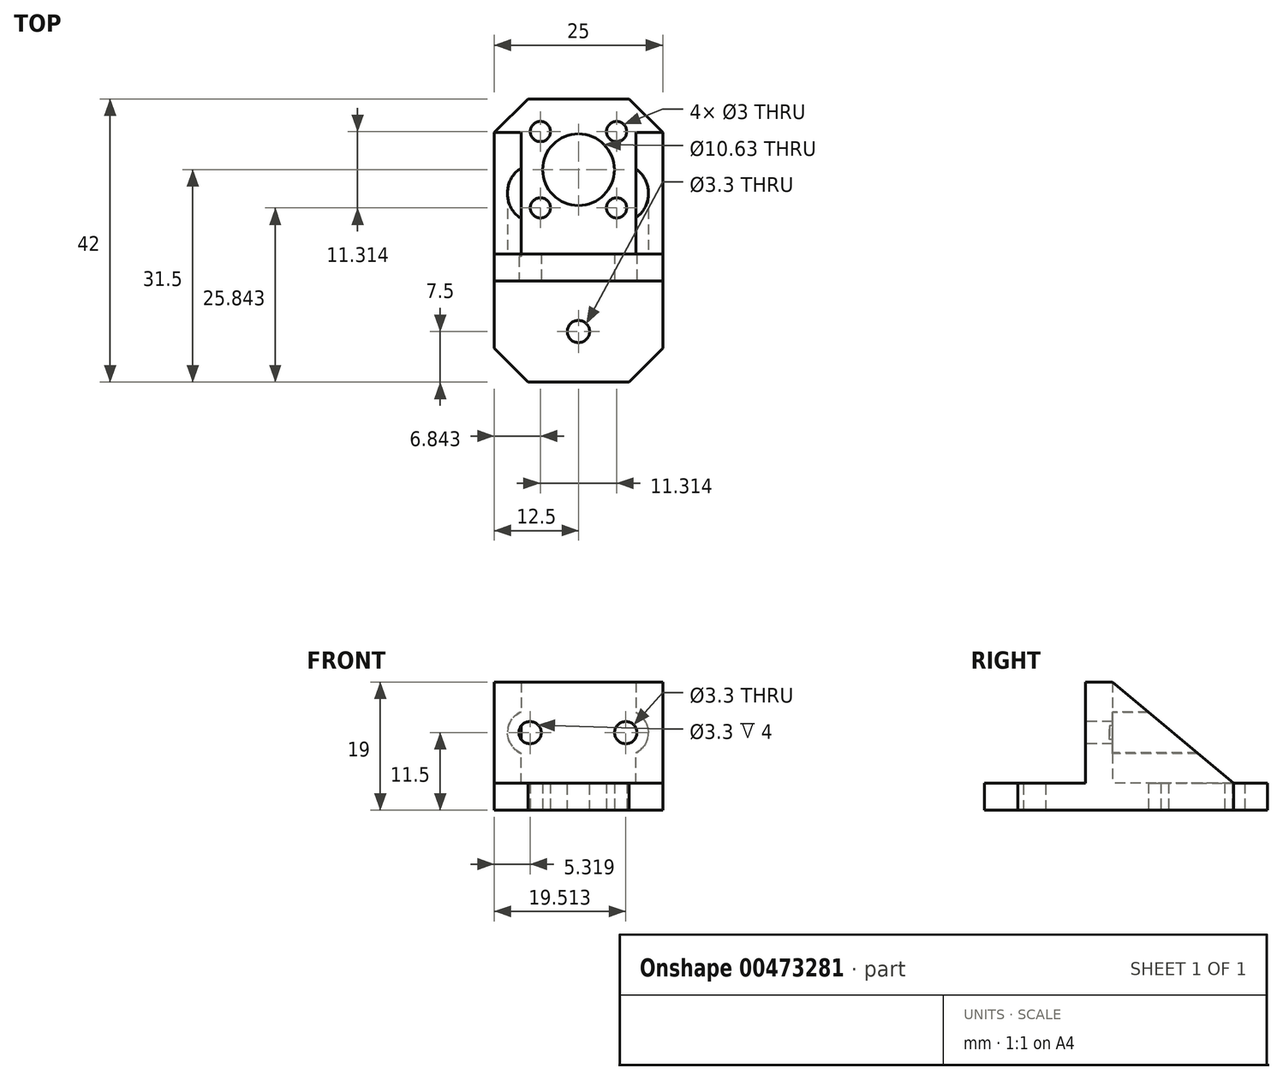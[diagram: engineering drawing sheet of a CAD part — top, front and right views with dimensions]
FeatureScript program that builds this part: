
annotation { "Feature Type Name" : "Feature", "Feature Type Description" : "" }
export const myFeature = defineFeature(function(context is Context, id is Id, definition is map)
    precondition{}
    {
        {
            var Q0;
            Q0=qCreatedBy(makeId("Top.planeOp"),FACE);
            var sketch = newSketch(context, id + "F0", { "sketchPlane" : qUnion([Q0])});
            skCircle(sketch, "E0.0", {"center": v(-5.66, 5.66) * mm, "radius": 1.5 * mm});
            skCircle(sketch, "E1.0", {"center": v(5.66, 5.66) * mm, "radius": 1.5 * mm});
            skCircle(sketch, "E2.0", {"center": v(0, 0) * mm, "radius": 5.32 * mm});
            skCircle(sketch, "E3.0", {"center": v(-5.66, -5.66) * mm, "radius": 1.5 * mm});
            skCircle(sketch, "E4.0", {"center": v(5.66, -5.66) * mm, "radius": 1.5 * mm});
            skLineSegment(sketch, "E5.MirrorCS", {"start": v(12.5, 10.5) * mm, "end": v(12.5, -10.5) * mm});
            skLineSegment(sketch, "E6.MirrorCS", {"start": v(10.5, -12.5) * mm, "end": v(-10.5, -12.5) * mm});
            skLineSegment(sketch, "E7.MirrorCS", {"start": v(-12.5, 10.5) * mm, "end": v(-12.5, -10.5) * mm});
            skPoint(sketch, "E8.visualSharp", {"position": v(-12.5, 12.5) * mm});
            skPoint(sketch, "E9.visualSharp", {"position": v(12.5, 12.5) * mm});
            skPoint(sketch, "E10.visualSharp", {"position": v(12.5, -12.5) * mm});
            skArc(sketch, "E10.filletArc", {"start": v(10.5, -12.5) * mm, "mid": v(11.91, -11.91) * mm, "end": v(12.5, -10.5) * mm});
            skPoint(sketch, "E11.visualSharp", {"position": v(-12.5, -12.5) * mm});
            skArc(sketch, "E11.filletArc", {"start": v(-12.5, -10.5) * mm, "mid": v(-11.91, -11.91) * mm, "end": v(-10.5, -12.5) * mm});
            skLineSegment(sketch, "E12.0", {"start": v(10.5, -16.5) * mm, "end": v(-10.5, -16.5) * mm});
            skLineSegment(sketch, "E13", {"start": v(-12.5, -10.5) * mm, "end": v(-12.5, -16.5) * mm});
            skLineSegment(sketch, "E14", {"start": v(-12.5, -16.5) * mm, "end": v(-10.5, -16.5) * mm});
            skLineSegment(sketch, "E15", {"start": v(10.5, -16.5) * mm, "end": v(12.5, -16.5) * mm});
            skLineSegment(sketch, "E16", {"start": v(12.5, -16.5) * mm, "end": v(12.5, -10.5) * mm});
            skLineSegment(sketch, "E17.bottom", {"start": v(-12.5, 10.5) * mm, "end": v(12.5, 10.5) * mm});
            skLineSegment(sketch, "E17.left", {"start": v(-12.5, 10.5) * mm, "end": v(-12.5, 10.5) * mm});
            skLineSegment(sketch, "E17.right", {"start": v(12.5, 10.5) * mm, "end": v(12.5, 10.5) * mm});
            skSolve(sketch);
        }
        {
            var Q0;
            Q0 = qSketchRegion(id + "F0", true);
            extrude(context, id + "F1", {"entities" : qUnion([Q0]), "depth" : 4 * mm, "offsetDistance" : 25 * mm});
        }
        {
            var Q0;
            Q0=makeQuery(id+"F1.opExtrude","SWEPT_EDGE",EDGE,{"disambiguationData":[OSD([sQuery(id+"F0.wireOp",EDGE,"E5.MirrorCS"),sQuery(id+"F0.wireOp",EDGE,"E17.bottom")])]});
            var Q1;
            Q1=makeQuery(id+"F1.opExtrude","SWEPT_EDGE",EDGE,{"disambiguationData":[OSD([sQuery(id+"F0.wireOp",EDGE,"E7.MirrorCS"),sQuery(id+"F0.wireOp",EDGE,"E17.bottom")])]});
            chamfer(context, id + "F2", {"entities" : qUnion([Q0, Q1]), "width" : 5 * mm, "tangentPropagation" : true});
        }
        {
            var Q0;
            Q0=makeQuery(id+"F1.opExtrude","CAP_FACE",FACE,{"disambiguationData":[OSD([sQuery(id+"F0.wireOp",EDGE,"E0.0"),sQuery(id+"F0.wireOp",EDGE,"E1.0"),sQuery(id+"F0.wireOp",EDGE,"E2.0"),sQuery(id+"F0.wireOp",EDGE,"E3.0"),sQuery(id+"F0.wireOp",EDGE,"E4.0"),sQuery(id+"F0.wireOp",EDGE,"E5.MirrorCS"),sQuery(id+"F0.wireOp",EDGE,"E7.MirrorCS"),sQuery(id+"F0.wireOp",EDGE,"E12.0"),sQuery(id+"F0.wireOp",EDGE,"E13"),sQuery(id+"F0.wireOp",EDGE,"E14"),sQuery(id+"F0.wireOp",EDGE,"E15"),sQuery(id+"F0.wireOp",EDGE,"E16"),sQuery(id+"F0.wireOp",EDGE,"E17.bottom")])],"isStart":false});
            var sketch = newSketch(context, id + "F3", { "sketchPlane" : qUnion([Q0])});
            skLineSegment(sketch, "E18.bottom", {"start": v(-12.5, -16.5) * mm, "end": v(12.5, -16.5) * mm});
            skLineSegment(sketch, "E18.top", {"start": v(-12.5, -12.5) * mm, "end": v(12.5, -12.5) * mm});
            skLineSegment(sketch, "E18.left", {"start": v(-12.5, -16.5) * mm, "end": v(-12.5, -12.5) * mm});
            skLineSegment(sketch, "E18.right", {"start": v(12.5, -16.5) * mm, "end": v(12.5, -12.5) * mm});
            skSolve(sketch);
        }
        {
            var Q0;
            Q0 = qSketchRegion(id + "F3", true);
            extrude(context, id + "F4", {"entities" : qUnion([Q0]), "operationType" : NewBodyOperationType.ADD, "depth" : 15 * mm, "offsetDistance" : 25 * mm});
        }
        {
            var Q0;
            Q0=makeQuery(id+"F1.opExtrude","CAP_FACE",FACE,{"disambiguationData":[OSD([sQuery(id+"F0.wireOp",EDGE,"E0.0"),sQuery(id+"F0.wireOp",EDGE,"E1.0"),sQuery(id+"F0.wireOp",EDGE,"E2.0"),sQuery(id+"F0.wireOp",EDGE,"E3.0"),sQuery(id+"F0.wireOp",EDGE,"E4.0"),sQuery(id+"F0.wireOp",EDGE,"E5.MirrorCS"),sQuery(id+"F0.wireOp",EDGE,"E7.MirrorCS"),sQuery(id+"F0.wireOp",EDGE,"E12.0"),sQuery(id+"F0.wireOp",EDGE,"E13"),sQuery(id+"F0.wireOp",EDGE,"E14"),sQuery(id+"F0.wireOp",EDGE,"E15"),sQuery(id+"F0.wireOp",EDGE,"E16"),sQuery(id+"F0.wireOp",EDGE,"E17.bottom")])],"isStart":true});
            var sketch = newSketch(context, id + "F5", { "sketchPlane" : qUnion([Q0])});
            skLineSegment(sketch, "E19.bottom", {"start": v(-12.5, 16.5) * mm, "end": v(12.5, 16.5) * mm});
            skLineSegment(sketch, "E19.top", {"start": v(-12.5, 31.5) * mm, "end": v(12.5, 31.5) * mm});
            skLineSegment(sketch, "E19.left", {"start": v(-12.5, 16.5) * mm, "end": v(-12.5, 31.5) * mm});
            skLineSegment(sketch, "E19.right", {"start": v(12.5, 16.5) * mm, "end": v(12.5, 31.5) * mm});
            skSolve(sketch);
        }
        {
            var Q0;
            Q0 = qSketchRegion(id + "F5", true);
            extrude(context, id + "F6", {"entities" : qUnion([Q0]), "operationType" : NewBodyOperationType.ADD, "oppositeDirection" : true, "depth" : 4 * mm, "offsetDistance" : 25 * mm});
        }
        {
            var Q0;
            Q0=makeQuery(id+"F4.boolean.opBoolean","MERGE",FACE,{"derivedFrom":[makeQuery(id+"F1.opExtrude","SWEPT_FACE",FACE,{"disambiguationData":[OSD([sQuery(id+"F0.wireOp",EDGE,"E12.0"),sQuery(id+"F0.wireOp",EDGE,"E14"),sQuery(id+"F0.wireOp",EDGE,"E15")])]}),makeQuery(id+"F4.opExtrude","SWEPT_FACE",FACE,{"disambiguationData":[OSD([sQuery(id+"F3.wireOp",EDGE,"E18.bottom")])]})]});
            var sketch = newSketch(context, id + "F7", { "sketchPlane" : qUnion([Q0])});
            skCircle(sketch, "E20", {"center": v(-7.18, 11.5) * mm, "radius": 1.65 * mm});
            skPoint(sketch, "E20.centerSnap0", {"position": v(-12.5, 11.5) * mm});
            skCircle(sketch, "E21", {"center": v(7.01, 11.5) * mm, "radius": 1.65 * mm});
            skSolve(sketch);
        }
        {
            var Q0;
            Q0 = qSketchRegion(id + "F7", true);
            extrude(context, id + "F8", {"entities" : qUnion([Q0]), "operationType" : NewBodyOperationType.REMOVE, "oppositeDirection" : true, "depth" : 25 * mm, "offsetDistance" : 25 * mm});
        }
        {
            var Q0;
            Q0=makeQuery(id+"F6.opExtrude","CAP_FACE",FACE,{"disambiguationData":[OSD([sQuery(id+"F5.wireOp",EDGE,"E19.bottom"),sQuery(id+"F5.wireOp",EDGE,"E19.top"),sQuery(id+"F5.wireOp",EDGE,"E19.left"),sQuery(id+"F5.wireOp",EDGE,"E19.right")])],"isStart":false});
            var sketch = newSketch(context, id + "F9", { "sketchPlane" : qUnion([Q0])});
            skCircle(sketch, "E22", {"center": v(0, -24) * mm, "radius": 1.65 * mm});
            skPoint(sketch, "E22.centerSnap0", {"position": v(0, -31.5) * mm});
            skPoint(sketch, "E22.centerSnap1", {"position": v(-12.5, -24) * mm});
            skSolve(sketch);
        }
        {
            var Q0;
            Q0 = qSketchRegion(id + "F9", true);
            extrude(context, id + "F10", {"entities" : qUnion([Q0]), "operationType" : NewBodyOperationType.REMOVE, "oppositeDirection" : true, "depth" : 25 * mm, "offsetDistance" : 25 * mm});
        }
        {
            var Q0;
            Q0=makeQuery(id+"F1.opExtrude","CAP_FACE",FACE,{"disambiguationData":[OSD([sQuery(id+"F0.wireOp",EDGE,"E0.0"),sQuery(id+"F0.wireOp",EDGE,"E1.0"),sQuery(id+"F0.wireOp",EDGE,"E2.0"),sQuery(id+"F0.wireOp",EDGE,"E3.0"),sQuery(id+"F0.wireOp",EDGE,"E4.0"),sQuery(id+"F0.wireOp",EDGE,"E5.MirrorCS"),sQuery(id+"F0.wireOp",EDGE,"E7.MirrorCS"),sQuery(id+"F0.wireOp",EDGE,"E12.0"),sQuery(id+"F0.wireOp",EDGE,"E13"),sQuery(id+"F0.wireOp",EDGE,"E14"),sQuery(id+"F0.wireOp",EDGE,"E15"),sQuery(id+"F0.wireOp",EDGE,"E16"),sQuery(id+"F0.wireOp",EDGE,"E17.bottom")])],"isStart":false});
            var sketch = newSketch(context, id + "F11", { "sketchPlane" : qUnion([Q0])});
            skLineSegment(sketch, "E23.bottom", {"start": v(-12.5, 5.5) * mm, "end": v(-8.5, 5.5) * mm});
            skLineSegment(sketch, "E23.top", {"start": v(-12.5, -12.92) * mm, "end": v(-8.5, -12.92) * mm});
            skLineSegment(sketch, "E23.left", {"start": v(-12.5, 5.5) * mm, "end": v(-12.5, -12.92) * mm});
            skLineSegment(sketch, "E23.right", {"start": v(-8.5, 5.5) * mm, "end": v(-8.5, -12.92) * mm});
            skLineSegment(sketch, "E24.bottom", {"start": v(12.5, 5.5) * mm, "end": v(8.5, 5.5) * mm});
            skLineSegment(sketch, "E24.top", {"start": v(12.5, -12.5) * mm, "end": v(8.5, -12.5) * mm});
            skLineSegment(sketch, "E24.left", {"start": v(12.5, 5.5) * mm, "end": v(12.5, -12.5) * mm});
            skLineSegment(sketch, "E24.right", {"start": v(8.5, 5.5) * mm, "end": v(8.5, -12.5) * mm});
            skSolve(sketch);
        }
        {
            var Q0;
            Q0 = qSketchRegion(id + "F11", true);
            var Q1;
            Q1=makeQuery(id+"F4.opExtrude","CAP_FACE",FACE,{"disambiguationData":[OSD([sQuery(id+"F3.wireOp",EDGE,"E18.bottom"),sQuery(id+"F3.wireOp",EDGE,"E18.top"),sQuery(id+"F3.wireOp",EDGE,"E18.left"),sQuery(id+"F3.wireOp",EDGE,"E18.right")])],"isStart":false});
            extrude(context, id + "F12", {"entities" : qUnion([Q0]), "operationType" : NewBodyOperationType.ADD, "endBound" : BoundingType.UP_TO_SURFACE, "depth" : 25 * mm, "endBoundEntityFace" : qUnion([Q1]), "offsetDistance" : 25 * mm});
        }
        {
            var Q0;
            Q0=makeQuery(id+"F12.boolean.opBoolean","MERGE",FACE,{"derivedFrom":[makeQuery(id+"F6.boolean.opBoolean","MERGE",FACE,{"derivedFrom":[makeQuery(id+"F4.boolean.opBoolean","MERGE",FACE,{"derivedFrom":[makeQuery(id+"F1.opExtrude","SWEPT_FACE",FACE,{"disambiguationData":[OSD([sQuery(id+"F0.wireOp",EDGE,"E7.MirrorCS"),sQuery(id+"F0.wireOp",EDGE,"E13")])]}),makeQuery(id+"F4.opExtrude","SWEPT_FACE",FACE,{"disambiguationData":[OSD([sQuery(id+"F3.wireOp",EDGE,"E18.left")])]})]}),makeQuery(id+"F6.opExtrude","SWEPT_FACE",FACE,{"disambiguationData":[OSD([sQuery(id+"F5.wireOp",EDGE,"E19.left")])]})]}),makeQuery(id+"F12.opExtrude","SWEPT_FACE",FACE,{"disambiguationData":[OSD([sQuery(id+"F11.wireOp",EDGE,"E23.left")])]})]});
            var sketch = newSketch(context, id + "F13", { "sketchPlane" : qUnion([Q0])});
            skPoint(sketch, "E25.0", {"position": v(-5.5, 4) * mm});
            skPoint(sketch, "E26.0", {"position": v(12.5, 19) * mm});
            skLineSegment(sketch, "E27", {"start": v(12.5, 19) * mm, "end": v(-5.5, 4) * mm});
            skLineSegment(sketch, "E28", {"start": v(-5.5, 19) * mm, "end": v(-5.5, 4) * mm});
            skLineSegment(sketch, "E29", {"start": v(12.5, 19) * mm, "end": v(-5.5, 19) * mm});
            skSolve(sketch);
        }
        {
            var Q0;
            Q0 = qSketchRegion(id + "F13", true);
            extrude(context, id + "F14", {"entities" : qUnion([Q0]), "operationType" : NewBodyOperationType.REMOVE, "oppositeDirection" : true, "depth" : 28.2 * mm, "offsetDistance" : 25 * mm});
        }
        {
            var Q0;
            Q0=makeQuery(id+"F4.opExtrude","SWEPT_FACE",FACE,{"disambiguationData":[OSD([sQuery(id+"F3.wireOp",EDGE,"E18.top")])]});
            var sketch = newSketch(context, id + "F15", { "sketchPlane" : qUnion([Q0])});
            skCircle(sketch, "E30", {"center": v(-7.01, 11.5) * mm, "radius": 3.35 * mm});
            skCircle(sketch, "E31", {"center": v(7.18, 11.5) * mm, "radius": 3.35 * mm});
            skSolve(sketch);
        }
        {
            var Q0;
            Q0 = qSketchRegion(id + "F15", true);
            extrude(context, id + "F16", {"entities" : qUnion([Q0]), "operationType" : NewBodyOperationType.REMOVE, "depth" : 25 * mm, "offsetDistance" : 25 * mm});
        }
        {
            var Q0;
            Q0=makeQuery(id+"F6.opExtrude","SWEPT_EDGE",EDGE,{"disambiguationData":[OSD([sQuery(id+"F5.wireOp",EDGE,"E19.top"),sQuery(id+"F5.wireOp",EDGE,"E19.left")])]});
            var Q1;
            Q1=makeQuery(id+"F6.opExtrude","SWEPT_EDGE",EDGE,{"disambiguationData":[OSD([sQuery(id+"F5.wireOp",EDGE,"E19.top"),sQuery(id+"F5.wireOp",EDGE,"E19.right")])]});
            chamfer(context, id + "F17", {"entities" : qUnion([Q0, Q1]), "width" : 5 * mm, "tangentPropagation" : true});
        }
    });
